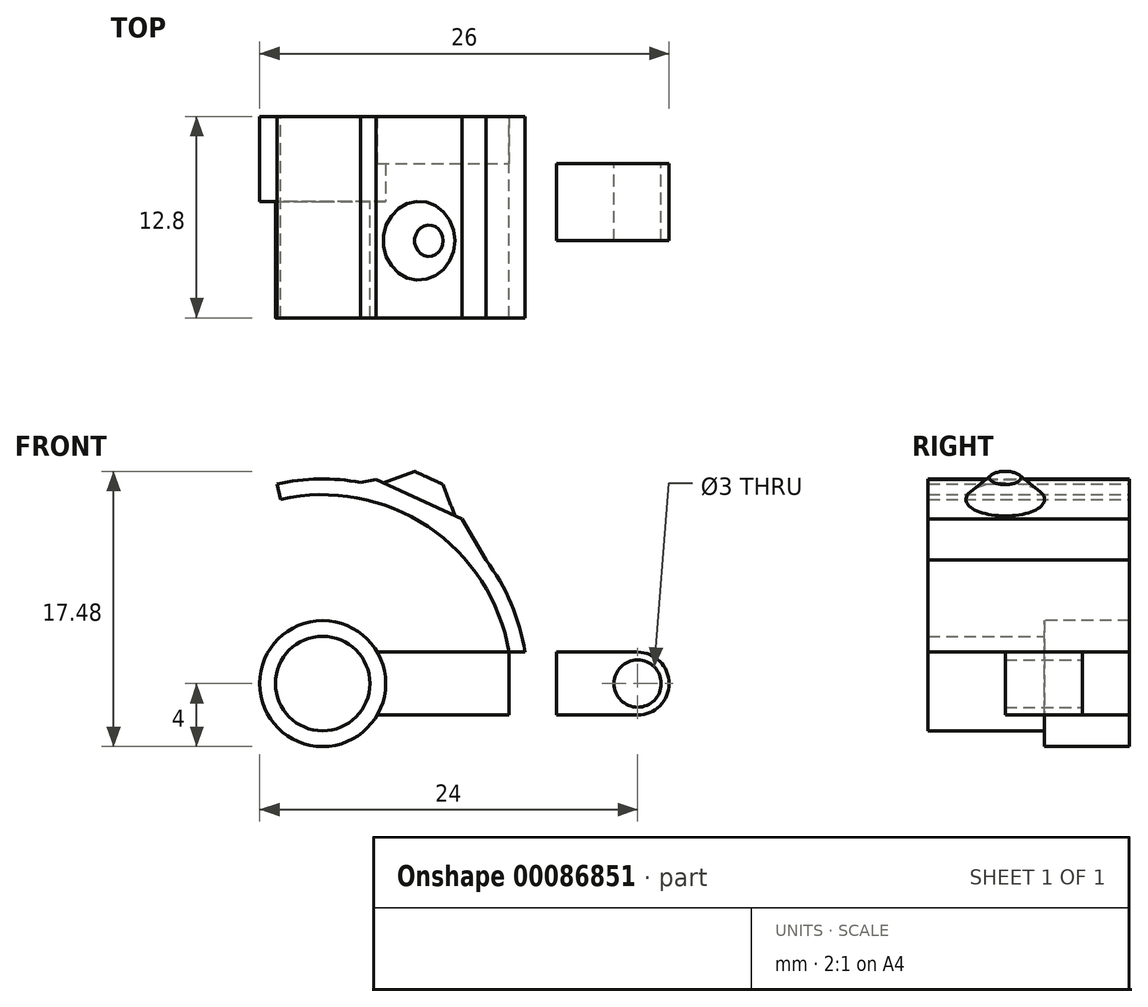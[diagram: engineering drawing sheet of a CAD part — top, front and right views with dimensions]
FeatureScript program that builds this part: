
annotation { "Feature Type Name" : "Feature", "Feature Type Description" : "" }
export const myFeature = defineFeature(function(context is Context, id is Id, definition is map)
    precondition{}
    {
        {
            var Q0;
            Q0=qCreatedBy(makeId("Front.planeOp"),FACE);
            var sketch = newSketch(context, id + "F0", { "sketchPlane" : qUnion([Q0])});
            skLineSegment(sketch, "E0", {"start": v(3.46, 2) * mm, "end": v(20, 2) * mm});
            skLineSegment(sketch, "E1", {"start": v(3.46, -2) * mm, "end": v(20, -2) * mm});
            skArc(sketch, "E2", {"start": v(3.46, 2) * mm, "mid": v(-4, 0) * mm, "end": v(3.46, -2) * mm});
            skArc(sketch, "E3", {"start": v(20, -2) * mm, "mid": v(22, 0) * mm, "end": v(20, 2) * mm});
            skCircle(sketch, "E4", {"center": v(0, 0) * mm, "radius": 3 * mm});
            skCircle(sketch, "E5", {"center": v(20, 0) * mm, "radius": 1.5 * mm});
            skArc(sketch, "E6", {"start": v(11.83, 2) * mm, "mid": v(6.67, 9.97) * mm, "end": v(-2.66, 11.7) * mm});
            skArc(sketch, "E7", {"start": v(12.85, 2) * mm, "mid": v(7.3, 10.76) * mm, "end": v(-2.88, 12.68) * mm});
            skCircle(sketch, "E8", {"center": v(0, 0) * mm, "radius": 11 * mm, "construction": true});
            skLineSegment(sketch, "E9", {"start": v(-2.88, 12.68) * mm, "end": v(-2.66, 11.7) * mm});
            skLineSegment(sketch, "E10.bottom", {"start": v(12.85, 2) * mm, "end": v(14.85, 2) * mm});
            skLineSegment(sketch, "E10.top", {"start": v(12.85, -2) * mm, "end": v(14.85, -2) * mm});
            skLineSegment(sketch, "E10.left", {"start": v(12.85, 2) * mm, "end": v(12.85, -2) * mm});
            skLineSegment(sketch, "E10.right", {"start": v(14.85, 2) * mm, "end": v(14.85, -2) * mm});
            skLineSegment(sketch, "E11.bottom", {"start": v(11.83, 2) * mm, "end": v(12.85, 2) * mm});
            skLineSegment(sketch, "E11.top", {"start": v(11.83, -2) * mm, "end": v(12.85, -2) * mm});
            skLineSegment(sketch, "E11.left", {"start": v(11.83, 2) * mm, "end": v(11.83, -2) * mm});
            skCircle(sketch, "E12", {"center": v(0, 0) * mm, "radius": 4 * mm});
            skLineSegment(sketch, "E13", {"start": v(2.4, 12.77) * mm, "end": v(3.4, 12.95) * mm});
            skLineSegment(sketch, "E14", {"start": v(8.84, 10.45) * mm, "end": v(10.36, 7.86) * mm});
            skLineSegment(sketch, "E15", {"start": v(3.4, 12.95) * mm, "end": v(8.84, 10.45) * mm});
            skLineSegment(sketch, "E16", {"start": v(0, 0) * mm, "end": v(-3.34, 14.66) * mm, "construction": true});
            skSolve(sketch);
        }
        {
            var Q0;
            Q0=makeQuery(id+"F0.imprint","IMPRINT",FACE,{"disambiguationData":[TD([[makeQuery(id+"F0.imprint","IMPRINT",EDGE,{"derivedFrom":sQuery(id+"F0.wireOp",EDGE,"E6")}),-1.0]])]});
            var Q1;
            Q1=makeQuery(id+"F0.imprint","IMPRINT",FACE,{"disambiguationData":[TD([[makeQuery(id+"F0.imprint","IMPRINT",EDGE,{"derivedFrom":sQuery(id+"F0.wireOp",EDGE,"E11.bottom")}),-1.0]])]});
            var Q2;
            {var subQ0=sQuery(id+"F0.wireOp",EDGE,"3pS9kvQB-MA37-qYVB-uYsJ-86lLepM1mav8");Q2=makeQuery(id+"F0.imprint","IMPRINT",FACE,{"disambiguationData":[TD([[makeQuery(id+"F0.imprint","IMPRINT",EDGE,{"derivedFrom":subQ0}),-1.0]])]});}
            var Q3;
            {var subQ0=sQuery(id+"F0.wireOp",EDGE,"JxdhKgBI-UXpi-5sW8-kgZY-4wMPMv5If6Lz");Q3=makeQuery(id+"F0.imprint","IMPRINT",FACE,{"disambiguationData":[TD([[makeQuery(id+"F0.imprint","IMPRINT",EDGE,{"derivedFrom":subQ0}),-1.0]])]});}
            var Q4;
            {var subQ0=sQuery(id+"F0.wireOp",EDGE,"SYK20XZZ-yXKu-EqdJ-Zuqa-4obpiRKccakK");Q4=makeQuery(id+"F0.imprint","IMPRINT",FACE,{"disambiguationData":[TD([[makeQuery(id+"F0.imprint","IMPRINT",EDGE,{"derivedFrom":subQ0}),-1.0]])]});}
            var Q5;
            {var subQ0=sQuery(id+"F0.wireOp",EDGE,"E13");Q5=makeQuery(id+"F0.imprint","IMPRINT",FACE,{"disambiguationData":[TD([[makeQuery(id+"F0.imprint","IMPRINT",EDGE,{"derivedFrom":subQ0}),-1.0]])]});}
            extrude(context, id + "F1", {"entities" : qUnion([Q0, Q1, Q2, Q3, Q4, Q5]), "depth" : 9.8 * mm});
        }
        {
            var Q0;
            Q0=makeQuery(id+"F0.imprint","IMPRINT",FACE,{"disambiguationData":[TD([[makeQuery(id+"F0.imprint","IMPRINT",EDGE,{"derivedFrom":sQuery(id+"F0.wireOp",EDGE,"E11.bottom")}),-1.0]])]});
            var Q1;
            {var subQ3=sQuery(id+"F0.wireOp",EDGE,"E11.left");Q1=makeQuery(id+"F0.imprint","IMPRINT",FACE,{"disambiguationData":[TD([[makeQuery(id+"F0.imprint","IMPRINT",EDGE,{"derivedFrom":subQ3}),-1.0]])]});}
            var Q2;
            Q2=makeQuery(id+"F0.imprint","IMPRINT",FACE,{"disambiguationData":[TD([[makeQuery(id+"F0.imprint","IMPRINT",EDGE,{"derivedFrom":sQuery(id+"F0.wireOp",EDGE,"E4")}),-1.0]])]});
            var Q3;
            Q3=makeQuery(id+"F0.imprint","IMPRINT",FACE,{"disambiguationData":[TD([[makeQuery(id+"F0.imprint","IMPRINT",EDGE,{"derivedFrom":sQuery(id+"F0.wireOp",EDGE,"E4")}),1.0]])]});
            extrude(context, id + "F2", {"entities" : qUnion([Q0, Q1, Q2, Q3]), "operationType" : NewBodyOperationType.ADD, "oppositeDirection" : true, "depth" : 3 * mm});
        }
        {
            var Q0;
            Q0=makeQuery(id+"F0.imprint","IMPRINT",FACE,{"disambiguationData":[TD([[makeQuery(id+"F0.imprint","IMPRINT",EDGE,{"derivedFrom":sQuery(id+"F0.wireOp",EDGE,"E10.bottom")}),-1.0]])]});
            var Q1;
            {var subQ0=sQuery(id+"F0.wireOp",EDGE,"E3");Q1=makeQuery(id+"F0.imprint","IMPRINT",FACE,{"disambiguationData":[TD([[makeQuery(id+"F0.imprint","IMPRINT",EDGE,{"derivedFrom":subQ0}),1.0]])]});}
            extrude(context, id + "F3", {"entities" : qUnion([Q0, Q1]), "operationType" : NewBodyOperationType.ADD, "depth" : 4.9 * mm});
        }
        {
            var Q0;
            Q0=makeQuery(id+"F2.opExtrude","CAP_FACE",FACE,{"disambiguationData":[OSD([sQuery(id+"F0.wireOp",EDGE,"E0"),sQuery(id+"F0.wireOp",EDGE,"E1"),sQuery(id+"F0.wireOp",EDGE,"E11.bottom"),sQuery(id+"F0.wireOp",EDGE,"E11.top"),sQuery(id+"F0.wireOp",EDGE,"E10.left"),sQuery(id+"F0.wireOp",EDGE,"E12")])],"isStart":true});
            var sketch = newSketch(context, id + "F4", { "sketchPlane" : qUnion([Q0])});
            skPoint(sketch, "E17", {"position": v(0, 0) * mm});
            skCircle(sketch, "E18", {"center": v(0, 0) * mm, "radius": 4 * mm});
            skLineSegment(sketch, "E19", {"start": v(3.46, 2) * mm, "end": v(11.83, 2) * mm});
            skLineSegment(sketch, "E20", {"start": v(11.83, 2) * mm, "end": v(11.83, -2) * mm});
            skLineSegment(sketch, "E21", {"start": v(11.83, -2) * mm, "end": v(3.46, -2) * mm});
            skCircle(sketch, "E22", {"center": v(0, 0) * mm, "radius": 3 * mm});
            skSolve(sketch);
        }
        {
            var Q0;
            Q0=makeQuery(id+"F4.imprint","IMPRINT",FACE,{"disambiguationData":[TD([[makeQuery(id+"F4.imprint","IMPRINT",EDGE,{"derivedFrom":sQuery(id+"F4.wireOp",EDGE,"E22")}),1.0]])]});
            extrude(context, id + "F5", {"entities" : qUnion([Q0]), "operationType" : NewBodyOperationType.ADD, "depth" : 9.8 * mm});
        }
        {
            var Q0;
            Q0=makeQuery(id+"F4.imprint","IMPRINT",FACE,{"disambiguationData":[TD([[makeQuery(id+"F4.imprint","IMPRINT",EDGE,{"derivedFrom":sQuery(id+"F4.wireOp",EDGE,"E22")}),-1.0]])]});
            extrude(context, id + "F6", {"entities" : qUnion([Q0]), "operationType" : NewBodyOperationType.ADD, "depth" : 2.4 * mm});
        }
        {
            var Q0;
            Q0=makeQuery(id+"F1.opExtrude","SWEPT_FACE",FACE,{"disambiguationData":[OSD([sQuery(id+"F0.wireOp",EDGE,"E15")])]});
            var sketch = newSketch(context, id + "F7", { "sketchPlane" : qUnion([Q0])});
            skLineSegment(sketch, "E23", {"start": v(-2.33, 0) * mm, "end": v(3.67, -9.8) * mm, "construction": true});
            skCircle(sketch, "E24", {"center": v(0.67, -4.9) * mm, "radius": 2.5 * mm});
            skSolve(sketch);
        }
        {
            var Q0;
            Q0 = qSketchRegion(id + "F7", true);
            extrude(context, id + "F8", {"entities" : qUnion([Q0]), "operationType" : NewBodyOperationType.ADD, "depth" : 1.5 * mm});
        }
        {
            var Q0;
            Q0=makeQuery(id+"F8.opExtrude","CAP_EDGE",EDGE,{"disambiguationData":[OSD([sQuery(id+"F7.wireOp",EDGE,"E24")])],"isStart":false});
            chamfer(context, id + "F9", {"entities" : qUnion([Q0]), "width" : 1.5 * mm, "tangentPropagation" : true});
        }
        {
            var Q0;
            Q0=makeQuery(id+"F1.opExtrude","CAP_FACE",FACE,{"disambiguationData":[OSD([sQuery(id+"F0.wireOp",EDGE,"E6"),sQuery(id+"F0.wireOp",EDGE,"E7"),sQuery(id+"F0.wireOp",EDGE,"E9"),sQuery(id+"F0.wireOp",EDGE,"E11.top"),sQuery(id+"F0.wireOp",EDGE,"E11.left"),sQuery(id+"F0.wireOp",EDGE,"E10.left"),sQuery(id+"F0.wireOp",EDGE,"E13"),sQuery(id+"F0.wireOp",EDGE,"E14"),sQuery(id+"F0.wireOp",EDGE,"E15")])],"isStart":true});
            extrude(context, id + "F10", {"entities" : qUnion([Q0]), "operationType" : NewBodyOperationType.ADD, "depth" : 3 * mm});
        }
    });
